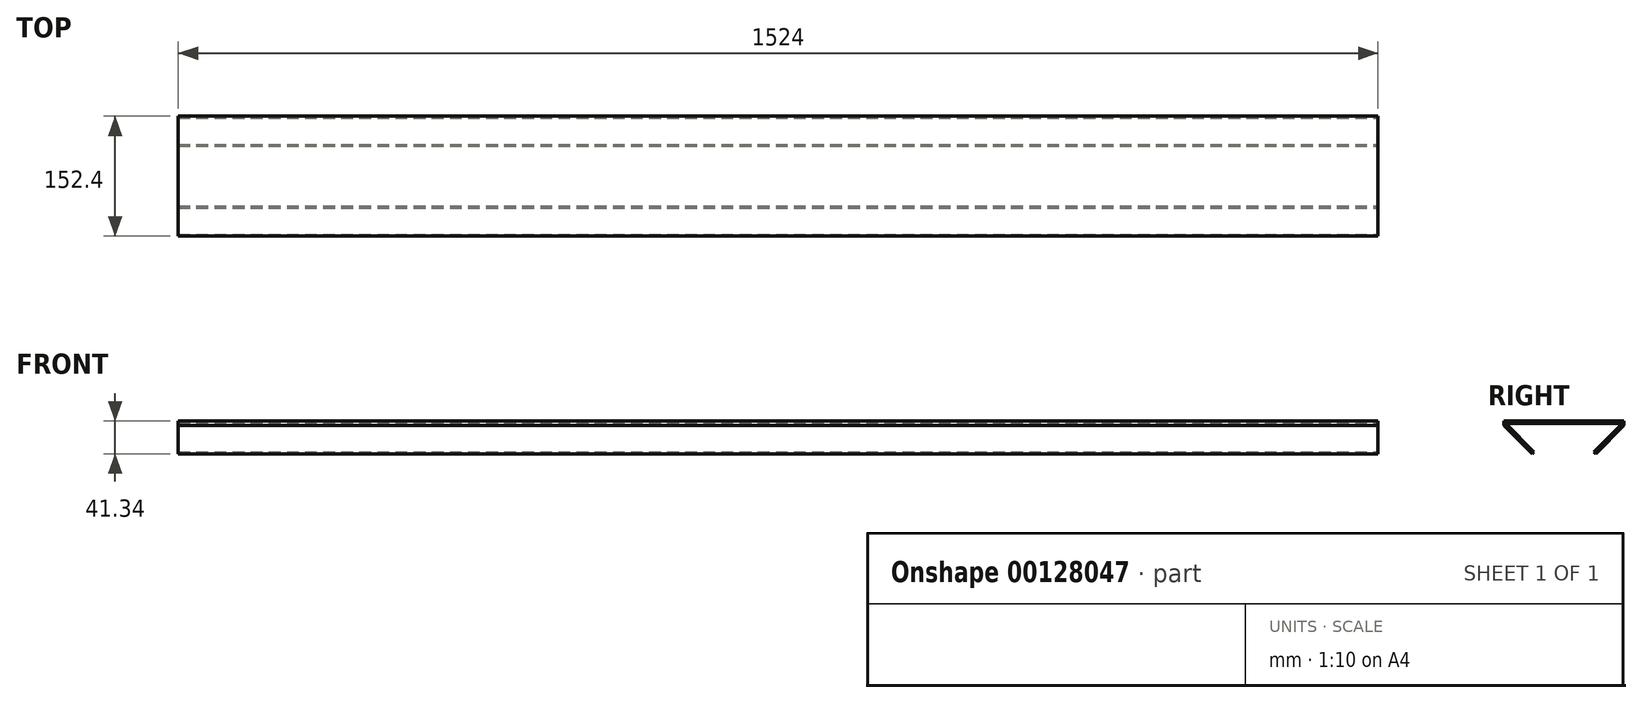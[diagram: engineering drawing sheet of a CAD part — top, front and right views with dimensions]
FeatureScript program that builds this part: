
annotation { "Feature Type Name" : "Feature", "Feature Type Description" : "" }
export const myFeature = defineFeature(function(context is Context, id is Id, definition is map)
    precondition{}
    {
        {
            var Q0;
            Q0=qCreatedBy(makeId("Right.planeOp"),FACE);
            var sketch = newSketch(context, id + "F0", { "sketchPlane" : qUnion([Q0])});
            skLineSegment(sketch, "E0.bottom", {"start": v(76.2, -1.59) * mm, "end": v(-76.2, -1.59) * mm});
            skLineSegment(sketch, "E0.top", {"start": v(76.2, 1.59) * mm, "end": v(-76.2, 1.59) * mm});
            skLineSegment(sketch, "E0.left", {"start": v(76.2, -1.59) * mm, "end": v(76.2, 1.59) * mm});
            skLineSegment(sketch, "E0.right", {"start": v(-76.2, -1.59) * mm, "end": v(-76.2, 1.59) * mm});
            skPoint(sketch, "E0.middle", {"position": v(0, 0) * mm});
            skLineSegment(sketch, "E1", {"start": v(73.95, -1.59) * mm, "end": v(76.2, -3.83) * mm});
            skLineSegment(sketch, "E2", {"start": v(76.2, -3.83) * mm, "end": v(40.28, -39.75) * mm});
            skLineSegment(sketch, "E3", {"start": v(73.95, -1.59) * mm, "end": v(38.03, -37.5) * mm});
            skLineSegment(sketch, "E4", {"start": v(40.28, -39.75) * mm, "end": v(38.03, -37.5) * mm});
            skLineSegment(sketch, "E5", {"start": v(-76.2, -3.83) * mm, "end": v(-40.28, -39.75) * mm});
            skLineSegment(sketch, "E6", {"start": v(-40.28, -39.75) * mm, "end": v(-38.03, -37.5) * mm});
            skLineSegment(sketch, "E7", {"start": v(-38.03, -37.5) * mm, "end": v(-73.95, -1.59) * mm});
            skLineSegment(sketch, "E8", {"start": v(-76.2, -3.83) * mm, "end": v(-73.95, -1.59) * mm});
            skLineSegment(sketch, "E9", {"start": v(-76.2, -1.59) * mm, "end": v(-76.2, -3.83) * mm});
            skLineSegment(sketch, "E10", {"start": v(76.2, -1.59) * mm, "end": v(76.2, -3.83) * mm});
            skSolve(sketch);
        }
        {
            var Q0;
            Q0 = qSketchRegion(id + "F0", true);
            extrude(context, id + "F1", {"entities" : qUnion([Q0]), "oppositeDirection" : true, "depth" : 1524 * mm});
        }
    });
